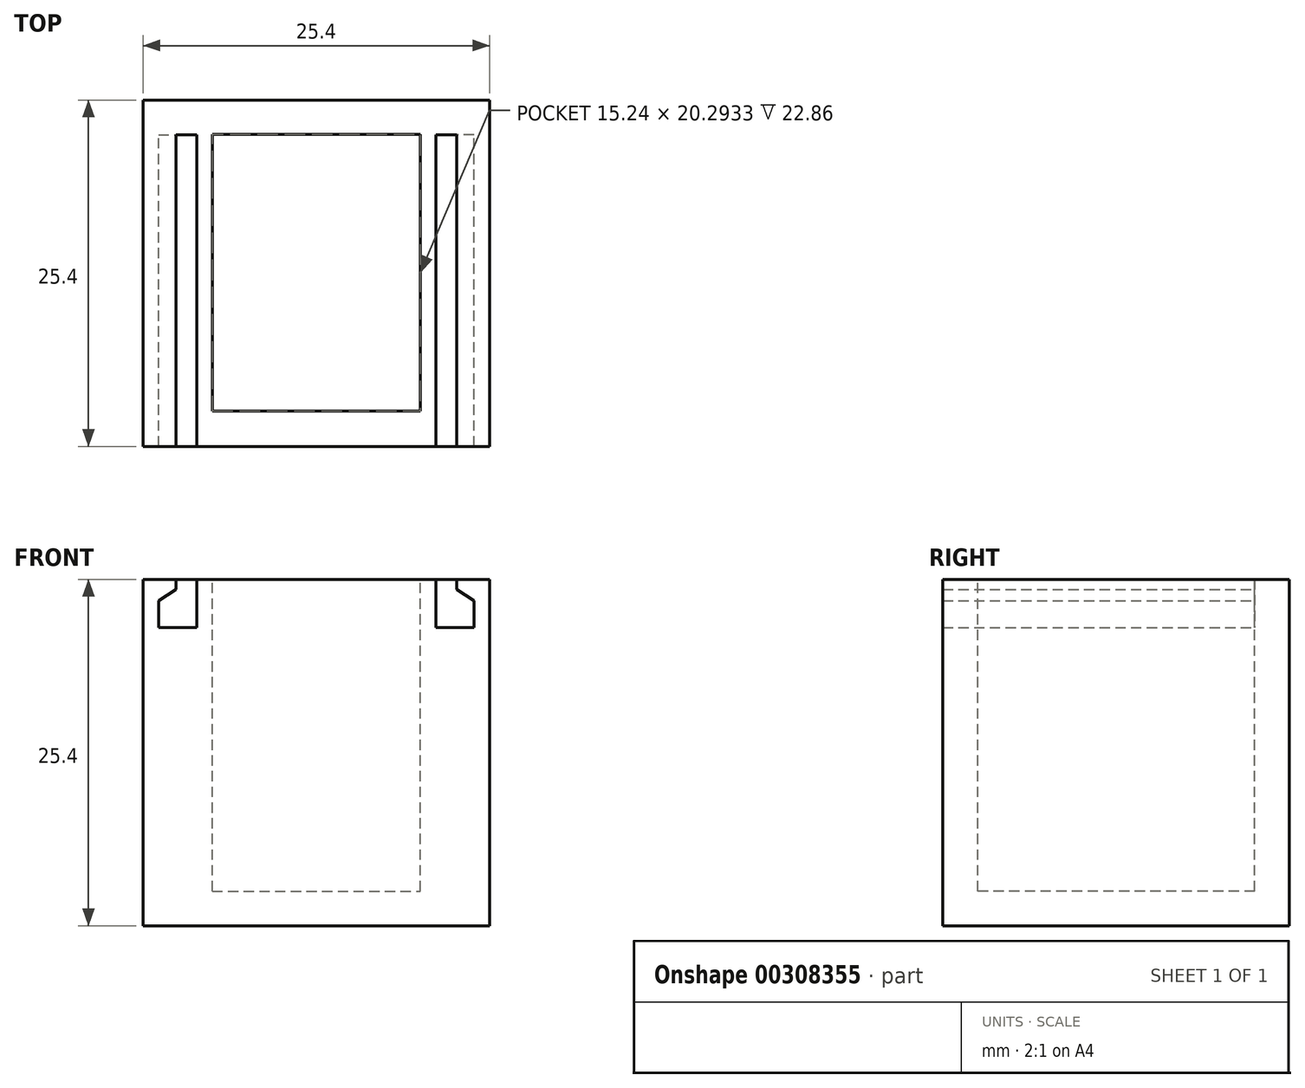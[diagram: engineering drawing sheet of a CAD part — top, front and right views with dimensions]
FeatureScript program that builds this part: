
annotation { "Feature Type Name" : "Feature", "Feature Type Description" : "" }
export const myFeature = defineFeature(function(context is Context, id is Id, definition is map)
    precondition{}
    {
        {
            var Q0;
            Q0=qCreatedBy(makeId("Top.planeOp"),FACE);
            var sketch = newSketch(context, id + "F0", { "sketchPlane" : qUnion([Q0])});
            skLineSegment(sketch, "E0.bottom", {"start": v(12.7, -12.7) * mm, "end": v(-12.7, -12.7) * mm});
            skLineSegment(sketch, "E0.top", {"start": v(12.7, 12.7) * mm, "end": v(-12.7, 12.7) * mm});
            skLineSegment(sketch, "E0.left", {"start": v(12.7, -12.7) * mm, "end": v(12.7, 12.7) * mm});
            skLineSegment(sketch, "E0.right", {"start": v(-12.7, -12.7) * mm, "end": v(-12.7, 12.7) * mm});
            skPoint(sketch, "E0.middle", {"position": v(0, 0) * mm});
            skSolve(sketch);
        }
        {
            var Q0;
            Q0=makeQuery(id+"F0.imprint","IMPRINT",FACE,{"disambiguationData":[TD([[makeQuery(id+"F0.imprint","IMPRINT",EDGE,{"derivedFrom":sQuery(id+"F0.wireOp",EDGE,"E0.bottom")}),-1.0]])]});
            extrude(context, id + "F1", {"entities" : qUnion([Q0]), "oppositeDirection" : true, "depth" : 25.4 * mm});
        }
        {
            var Q0;
            Q0=qCreatedBy(makeId("Top.planeOp"),FACE);
            var sketch = newSketch(context, id + "F2", { "sketchPlane" : qUnion([Q0])});
            skPoint(sketch, "E1.middle", {"position": v(0, 0) * mm});
            skLineSegment(sketch, "E2", {"start": v(-7.62, 10.17) * mm, "end": v(7.62, 10.17) * mm});
            skLineSegment(sketch, "E3", {"start": v(-7.62, -10.13) * mm, "end": v(7.62, -10.13) * mm});
            skLineSegment(sketch, "E4", {"start": v(-7.62, 10.17) * mm, "end": v(-7.62, -10.13) * mm});
            skLineSegment(sketch, "E5", {"start": v(7.62, 10.17) * mm, "end": v(7.62, -10.13) * mm});
            skSolve(sketch);
        }
        {
            var Q0;
            Q0=qSketchRegion(id+"F2",true);
            extrude(context, id + "F3", {"entities" : qUnion([Q0]), "operationType" : NewBodyOperationType.REMOVE, "oppositeDirection" : true, "depth" : 22.86 * mm});
        }
        {
            var Q0;
            Q0=qCreatedBy(makeId("Front.planeOp"),FACE);
            var sketch = newSketch(context, id + "F4", { "sketchPlane" : qUnion([Q0])});
            skLineSegment(sketch, "E6.1", {"start": v(11.56, -3.55) * mm, "end": v(8.76, -3.55) * mm});
            skLineSegment(sketch, "E6.2", {"start": v(11.56, -3.55) * mm, "end": v(11.56, -1.57) * mm});
            skLineSegment(sketch, "E6.4", {"start": v(11.56, -1.57) * mm, "end": v(10.28, -0.74) * mm});
            skLineSegment(sketch, "E7", {"start": v(10.28, -0.74) * mm, "end": v(10.28, 0) * mm});
            skLineSegment(sketch, "E8", {"start": v(8.76, 0) * mm, "end": v(8.76, -3.55) * mm});
            skLineSegment(sketch, "E9", {"start": v(8.76, 0) * mm, "end": v(10.28, 0) * mm});
            skLineSegment(sketch, "E10.MirrorCS", {"start": v(-8.76, 0) * mm, "end": v(-8.76, -3.55) * mm});
            skLineSegment(sketch, "E11.MirrorCS", {"start": v(-8.76, 0) * mm, "end": v(-10.28, 0) * mm});
            skLineSegment(sketch, "E12.MirrorCS", {"start": v(-10.28, -0.74) * mm, "end": v(-10.28, 0) * mm});
            skLineSegment(sketch, "E13.MirrorCS", {"start": v(-11.56, -1.57) * mm, "end": v(-10.28, -0.74) * mm});
            skLineSegment(sketch, "E14.MirrorCS", {"start": v(-11.56, -3.55) * mm, "end": v(-11.56, -1.57) * mm});
            skLineSegment(sketch, "E15.MirrorCS", {"start": v(-11.56, -3.55) * mm, "end": v(-8.76, -3.55) * mm});
            skSolve(sketch);
        }
        {
            var Q0;
            Q0=qCreatedBy(makeId("Right.planeOp"),FACE);
            var sketch = newSketch(context, id + "F5", { "sketchPlane" : qUnion([Q0])});
            skLineSegment(sketch, "E16", {"start": v(12.7, 0) * mm, "end": v(12.7, -3.8) * mm});
            skLineSegment(sketch, "E17", {"start": v(12.7, -3.8) * mm, "end": v(10.16, -3.8) * mm});
            skLineSegment(sketch, "E18", {"start": v(10.16, -3.8) * mm, "end": v(10.16, 0) * mm});
            skLineSegment(sketch, "E19", {"start": v(10.16, 0) * mm, "end": v(12.7, 0) * mm});
            skSolve(sketch);
        }
        {
            var Q0;
            Q0=makeQuery(id+"F4.imprint","IMPRINT",FACE,{"disambiguationData":[TD([[makeQuery(id+"F4.imprint","IMPRINT",EDGE,{"derivedFrom":sQuery(id+"F4.wireOp",EDGE,"E10.MirrorCS")}),-1.0]])]});
            var Q1;
            Q1=makeQuery(id+"F4.imprint","IMPRINT",FACE,{"disambiguationData":[TD([[makeQuery(id+"F4.imprint","IMPRINT",EDGE,{"derivedFrom":sQuery(id+"F4.wireOp",EDGE,"E6.1")}),-1.0]])]});
            extrude(context, id + "F6", {"entities" : qUnion([Q0, Q1]), "operationType" : NewBodyOperationType.REMOVE, "depth" : 25.4 * mm, "symmetric" : true});
        }
        {
            var Q0;
            Q0=makeQuery(id+"F5.imprint","IMPRINT",FACE,{"disambiguationData":[TD([[makeQuery(id+"F5.imprint","IMPRINT",EDGE,{"derivedFrom":sQuery(id+"F5.wireOp",EDGE,"E16")}),-1.0]])]});
            extrude(context, id + "F7", {"entities" : qUnion([Q0]), "operationType" : NewBodyOperationType.ADD, "depth" : 25.4 * mm, "symmetric" : true});
        }
    });
